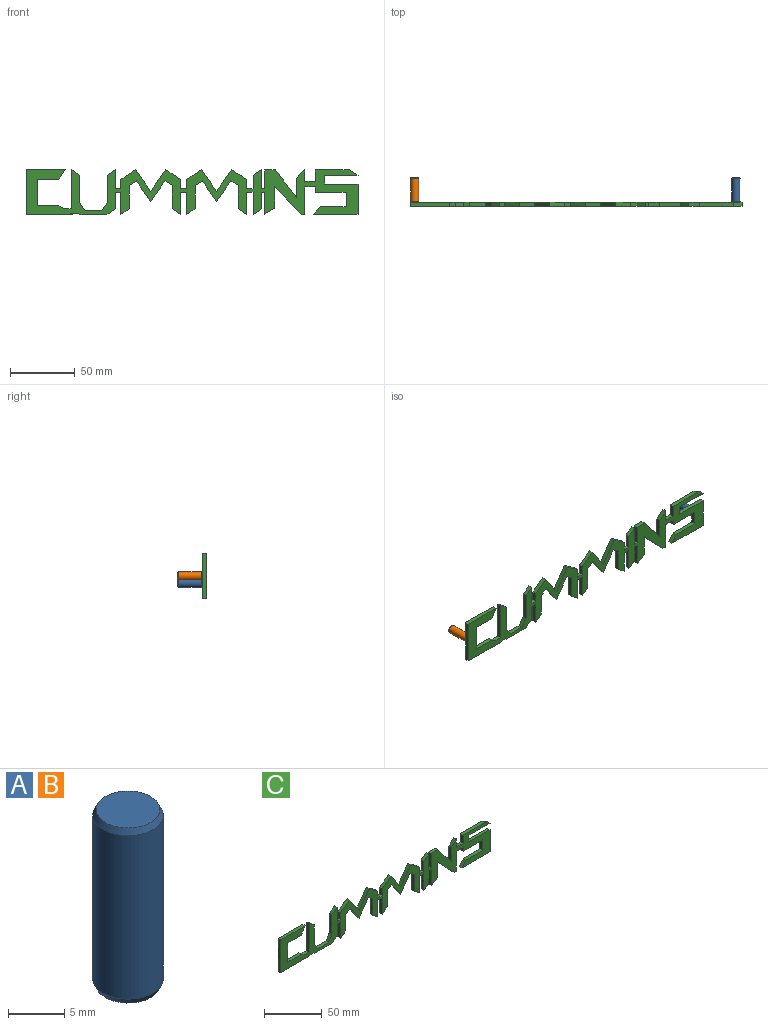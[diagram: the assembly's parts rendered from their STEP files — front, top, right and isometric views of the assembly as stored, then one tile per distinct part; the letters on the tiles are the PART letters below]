
ASSEMBLY  parts=3 mates=2
PART A: 5 faces, bbox 6.3x6.3x19.1 mm
  f0: plane 5.68x5.68mm, normal (0,0,1), area 25.4mm2, adj f1
  f1: cone r=2.84mm half-angle=25deg, axis (0,0,-1), area 13.2mm2, adj f0,f2
  f2: cylinder r=3.14mm len=17.78mm, axis (0,0,-1), area 350.4mm2, adj f1,f3
  f3: cone r=3.14mm half-angle=25deg, axis (0,0,1), area 13.2mm2, adj f2,f4
  f4: plane 5.68x5.68mm, normal (0,0,-1), area 25.4mm2, adj f3
PART B: same geometry as A
PART C: 99 faces, bbox 257.2x3.2x35 mm
  f0: plane 7.57x4.85mm, normal (0.84,0,-0.54), area 28.5mm2, adj f1,f96,f97,f98
  f1: plane 30.36x3.18mm, normal (0,0,1), area 96.4mm2, adj f0,f2,f97,f98
  f2: plane 34.88x3.18mm, normal (-1,0,0), area 110.7mm2, adj f1,f3,f97,f98
  f3: plane 36.05x3.18mm, normal (0,0,-1), area 114.5mm2, adj f2,f4,f97,f98
  f4: plane 3.18x1.48mm, normal (0.54,0,0.84), area 5.6mm2, adj f3,f5,f97,f98
  f5: plane 5.64x3.18mm, normal (0,0,-1), area 17.9mm2, adj f4,f6,f97,f98
  f6: plane 3.18x1.58mm, normal (-0.57,0,-0.82), area 6.1mm2, adj f5,f7,f97,f98
  f7: plane 20.91x3.18mm, normal (0,0,-1), area 66.4mm2, adj f6,f8,f97,f98
  f8: plane 6.78x4.71mm, normal (0.57,0,-0.82), area 26.2mm2, adj f7,f9,f97,f98
  f9: plane 12.78x3.18mm, normal (1,0,0), area 40.6mm2, adj f8,f10,f97,f98
  f10: plane 4.05x3.18mm, normal (0,0,-1), area 12.9mm2, adj f9,f11,f97,f98
  f11: plane 17.5x3.18mm, normal (-1,0,0), area 55.6mm2, adj f10,f12,f97,f98
  f12: plane 6.35x4.71mm, normal (0.6,0,-0.8), area 25.1mm2, adj f11,f13,f97,f98
  f13: plane 17.68x3.18mm, normal (1,0,0), area 56.1mm2, adj f12,f14,f97,f98
  f14: plane 5.49x3.82mm, normal (0.57,0,-0.82), area 21.2mm2, adj f13,f15,f97,f98
  f15: plane 16.09x11.18mm, normal (-0.82,0,-0.57), area 62.2mm2, adj f14,f16,f97,f98
  f16: plane 16.09x11.18mm, normal (0.82,0,-0.57), area 62.2mm2, adj f15,f17,f97,f98
  f17: plane 5.49x3.82mm, normal (-0.57,0,-0.82), area 21.2mm2, adj f16,f18,f97,f98
  f18: plane 17.68x3.18mm, normal (-1,0,0), area 56.1mm2, adj f17,f19,f97,f98
  f19: plane 6.35x4.71mm, normal (-0.6,0,-0.8), area 25.1mm2, adj f18,f20,f97,f98
  f20: plane 17.5x3.18mm, normal (1,0,0), area 55.6mm2, adj f19,f21,f97,f98
  f21: plane 5.03x3.18mm, normal (0,0,-1), area 16mm2, adj f20,f22,f97,f98
  f22: plane 17.5x3.18mm, normal (-1,0,0), area 55.6mm2, adj f21,f23,f97,f98
  f23: plane 6.35x4.71mm, normal (0.6,0,-0.8), area 25.1mm2, adj f22,f24,f97,f98
  f24: plane 17.68x3.18mm, normal (1,0,0), area 56.1mm2, adj f23,f25,f97,f98
  f25: plane 5.49x3.82mm, normal (0.57,0,-0.82), area 21.2mm2, adj f24,f26,f97,f98
  f26: plane 16.09x11.18mm, normal (-0.82,0,-0.57), area 62.2mm2, adj f25,f27,f97,f98
  f27: plane 16.09x11.18mm, normal (0.82,0,-0.57), area 62.2mm2, adj f26,f28,f97,f98
  f28: plane 5.49x3.82mm, normal (-0.57,0,-0.82), area 21.2mm2, adj f27,f29,f97,f98
  f29: plane 17.68x3.18mm, normal (-1,0,0), area 56.1mm2, adj f28,f30,f97,f98
  f30: plane 6.35x4.71mm, normal (-0.6,0,-0.8), area 25.1mm2, adj f29,f31,f97,f98
  f31: plane 17.5x3.18mm, normal (1,0,0), area 55.6mm2, adj f30,f32,f97,f98
  f32: plane 5.22x3.18mm, normal (0,0,-1), area 16.6mm2, adj f31,f33,f97,f98
  f33: plane 17.5x3.18mm, normal (-1,0,0), area 55.6mm2, adj f32,f34,f97,f98
  f34: plane 6.35x4.41mm, normal (0.57,0,-0.82), area 24.6mm2, adj f33,f35,f97,f98
  f35: plane 13.08x3.18mm, normal (1,0,0), area 41.5mm2, adj f34,f36,f97,f98
  f36: plane 3.18x2.73mm, normal (0,0,-1), area 8.7mm2, adj f35,f37,f97,f98
  f37: plane 17.1x3.18mm, normal (-1,0,-0.01), area 54.3mm2, adj f36,f38,f97,f98
  f38: plane 7.85x4.62mm, normal (0.51,0,-0.86), area 28.9mm2, adj f37,f39,f97,f98
  f39: plane 16.56x3.18mm, normal (1,0,0), area 52.6mm2, adj f38,f40,f97,f98
  f40: plane 21.36x20.27mm, normal (-0.73,0,-0.69), area 93.5mm2, adj f39,f41,f97,f98
  f41: plane 3.18x2.8mm, normal (0,0,-1), area 8.9mm2, adj f40,f42,f97,f98
  f42: plane 21.18x3.18mm, normal (1,0,0), area 67.2mm2, adj f41,f43,f97,f98
  f43: plane 8.26x3.18mm, normal (0,0,-1), area 26.2mm2, adj f42,f44,f97,f98
  f44: plane 3.97x3.18mm, normal (-1,0,0), area 12.6mm2, adj f43,f45,f97,f98
  f45: plane 23.76x3.18mm, normal (0,0,-1), area 75.4mm2, adj f44,f46,f97,f98
  f46: plane 11.15x3.18mm, normal (-1,0,0), area 35.4mm2, adj f45,f47,f97,f98
  f47: plane 20.12x3.18mm, normal (0,0,1), area 63.9mm2, adj f46,f48,f97,f98
  f48: plane 6.06x5mm, normal (-0.77,0,0.64), area 24.9mm2, adj f47,f49,f97,f98
  f49: plane 34.35x3.18mm, normal (0,0,-1), area 109.1mm2, adj f48,f50,f97,f98
  f50: plane 23.41x3.18mm, normal (1,0,0), area 74.3mm2, adj f49,f51,f97,f98
  f51: plane 25.87x3.18mm, normal (0,0,1), area 82.1mm2, adj f50,f52,f97,f98
  f52: plane 6.87x3.18mm, normal (1,0,0), area 21.8mm2, adj f51,f53,f97,f98
  f53: plane 25.87x3.18mm, normal (0,0,-1), area 82.1mm2, adj f52,f54,f97,f98
  f54: plane 6.88x4.13mm, normal (0.51,0,0.86), area 25.5mm2, adj f53,f55,f97,f98
  f55: plane 26.11x3.18mm, normal (0,0,1), area 82.9mm2, adj f54,f56,f97,f98
  f56: plane 8.95x3.18mm, normal (-1,0,0), area 28.4mm2, adj f55,f57,f97,f98
  f57: plane 8.26x3.18mm, normal (0,0,1), area 26.2mm2, adj f56,f58,f97,f98
  f58: plane 8.95x3.18mm, normal (1,0,0), area 28.4mm2, adj f57,f59,f97,f98
  f59: plane 6.28x6.27mm, normal (-0.71,0,0.71), area 28.2mm2, adj f58,f60,f97,f98
  f60: plane 14.81x3.18mm, normal (-1,0,0), area 47mm2, adj f59,f61,f97,f98
  f61: plane 21.09x16.7mm, normal (0.78,0,0.62), area 85.4mm2, adj f60,f62,f97,f98
  f62: plane 8.15x3.18mm, normal (-0.01,0,1), area 25.9mm2, adj f61,f63,f97,f98
  f63: plane 14.71x3.18mm, normal (-1,0,-0.01), area 46.7mm2, adj f62,f64,f97,f98
  f64: plane 3.18x2.71mm, normal (0,0,1), area 8.6mm2, adj f63,f65,f97,f98
  f65: plane 15.15x3.18mm, normal (1,0,0), area 48.1mm2, adj f64,f66,f97,f98
  f66: plane 6.35x4.41mm, normal (-0.57,0,0.82), area 24.6mm2, adj f65,f67,f97,f98
  f67: plane 10.74x3.18mm, normal (-1,0,0), area 34.1mm2, adj f66,f68,f97,f98
  f68: plane 5.22x3.18mm, normal (0,0,1), area 16.6mm2, adj f67,f69,f97,f98
  f69: plane 7.34x3.18mm, normal (1,0,0), area 23.3mm2, adj f68,f70,f97,f98
  f70: plane 11.24x7.81mm, normal (0.57,0,0.82), area 43.5mm2, adj f69,f71,f97,f98
  f71: plane 16.95x11.78mm, normal (-0.82,0,0.57), area 65.5mm2, adj f70,f72,f97,f98
  f72: plane 16.95x11.78mm, normal (0.82,0,0.57), area 65.5mm2, adj f71,f73,f97,f98
  f73: plane 11.24x7.81mm, normal (-0.57,0,0.82), area 43.5mm2, adj f72,f74,f97,f98
  f74: plane 7.34x3.18mm, normal (-1,0,0), area 23.3mm2, adj f73,f75,f97,f98
  f75: plane 5.03x3.18mm, normal (0,0,1), area 16mm2, adj f74,f76,f97,f98
  f76: plane 7.34x3.18mm, normal (1,0,0), area 23.3mm2, adj f75,f77,f97,f98
  f77: plane 11.24x7.81mm, normal (0.57,0,0.82), area 43.5mm2, adj f76,f78,f97,f98
  f78: plane 16.95x11.78mm, normal (-0.82,0,0.57), area 65.5mm2, adj f77,f79,f97,f98
  f79: plane 16.95x11.78mm, normal (0.82,0,0.57), area 65.5mm2, adj f78,f80,f97,f98
  f80: plane 11.24x7.81mm, normal (-0.57,0,0.82), area 43.5mm2, adj f79,f81,f97,f98
  f81: plane 7.34x3.18mm, normal (-1,0,0), area 23.3mm2, adj f80,f82,f97,f98
  f82: plane 4.05x3.18mm, normal (0,0,1), area 12.9mm2, adj f81,f83,f97,f98
  f83: plane 15.15x3.18mm, normal (1,0,0), area 48.1mm2, adj f82,f84,f97,f98
  f84: plane 6.35x4.6mm, normal (-0.59,0,0.81), area 24.9mm2, adj f83,f85,f97,f98
  f85: plane 21.02x3.18mm, normal (-1,0,0), area 66.7mm2, adj f84,f86,f97,f98
  f86: plane 6.45x4.41mm, normal (-0.83,0,0.56), area 24.8mm2, adj f85,f87,f97,f98
  f87: plane 12.95x3.18mm, normal (0,0,1), area 41.1mm2, adj f86,f88,f97,f98
  f88: plane 6.45x4.41mm, normal (0.83,0,0.56), area 24.8mm2, adj f87,f89,f97,f98
  f89: plane 21.02x3.18mm, normal (1,0,0), area 66.7mm2, adj f88,f90,f97,f98
  f90: plane 6.35x4.6mm, normal (0.59,0,0.81), area 24.9mm2, adj f89,f91,f97,f98
  f91: plane 30.31x3.18mm, normal (-1,0,0), area 96.2mm2, adj f90,f92,f97,f98
  f92: plane 6.02x3.18mm, normal (0,0,1), area 19.1mm2, adj f91,f93,f97,f98
  f93: plane 3.47x3.18mm, normal (0.54,0,0.84), area 13.1mm2, adj f92,f94,f97,f98
  f94: plane 16.55x3.18mm, normal (0,0,1), area 52.5mm2, adj f93,f95,f97,f98
  f95: plane 20.5x3.18mm, normal (1,0,0), area 65.1mm2, adj f94,f96,f97,f98
  f96: plane 16.55x3.18mm, normal (0,0,-1), area 52.5mm2, adj f0,f95,f97,f98
  f97: plane 257.22x35.02mm, normal (0,-1,0), area 3923.3mm2, adj f0,f1,f2,f3,f4,f5,f6,f7
  f98: plane 257.22x35.02mm, normal (0,1,0), area 3923.3mm2, adj f0,f1,f2,f3,f4,f5,f6,f7
PLACE A rot(axis=(1,0,0),90deg) t=(-14.21,6.35,19.91)mm
PLACE B rot(axis=(1,0,0),90deg) t=(-263.21,6.35,25.65)mm
PLACE C at identity
MATE fastened A.f1 <-> C.f98  axis (0,-1,0) through (-14.21,-3.18,19.91)mm
MATE fastened B.f1 <-> C.f98  axis (0,-1,0) through (-263.21,-3.18,25.65)mm
